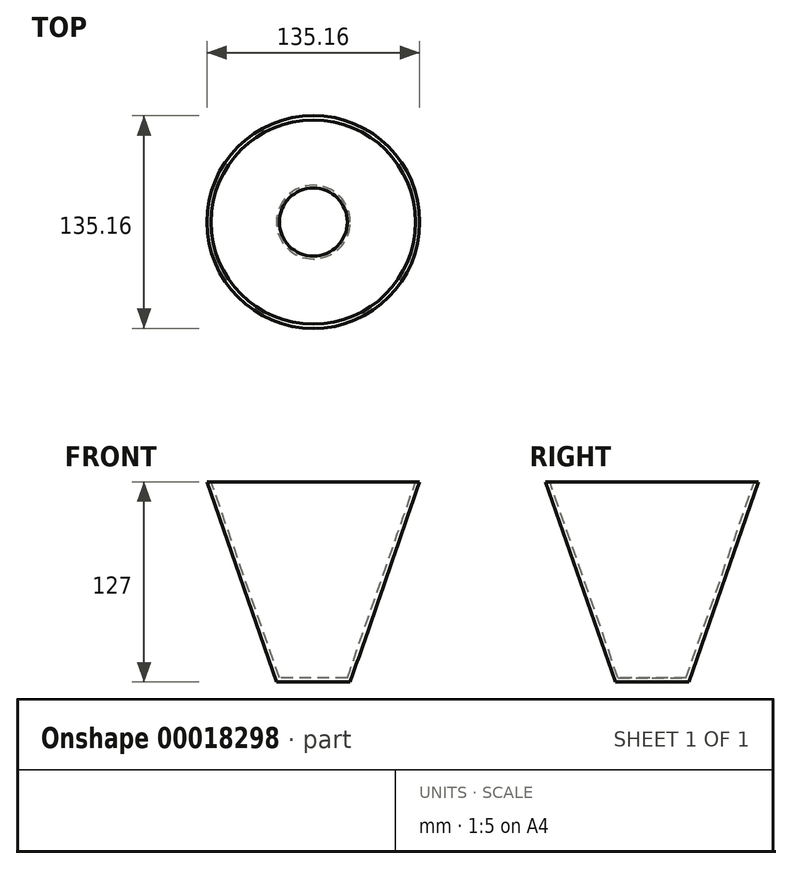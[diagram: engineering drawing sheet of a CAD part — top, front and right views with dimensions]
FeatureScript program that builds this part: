
annotation { "Feature Type Name" : "Feature", "Feature Type Description" : "" }
export const myFeature = defineFeature(function(context is Context, id is Id, definition is map)
    precondition{}
    {
        {
            var Q0;
            Q0=qCreatedBy(makeId("Top.planeOp"),FACE);
            cPlane(context, id + "F0", {"entities" : qUnion([Q0]), "cplaneType" : CPlaneType.OFFSET, "offset" : 127 * mm, "width" : 152.4 * mm, "height" : 152.4 * mm});
        }
        {
            var Q0;
            Q0=qCreatedBy(makeId("Top.planeOp"),FACE);
            var sketch = newSketch(context, id + "F1", { "sketchPlane" : qUnion([Q0])});
            skCircle(sketch, "E0", {"center": v(0, 0) * mm, "radius": 23.42 * mm});
            skSolve(sketch);
        }
        {
            var Q0;
            Q0=qCreatedBy(id+"F0.planeOp",FACE);
            var sketch = newSketch(context, id + "F2", { "sketchPlane" : qUnion([Q0])});
            skPoint(sketch, "E1", {"position": v(0, 0) * mm});
            skCircle(sketch, "E2", {"center": v(0, 0) * mm, "radius": 67.58 * mm});
            skSolve(sketch);
        }
        {
            var Q0;
            Q0=makeQuery(id+"F2.imprint","IMPRINT",FACE,{"disambiguationData":[TD([[makeQuery(id+"F2.imprint","IMPRINT",EDGE,{"derivedFrom":sQuery(id+"F2.wireOp",EDGE,"E2")}),1.0]])]});
            var Q1;
            Q1=makeQuery(id+"F1.imprint","IMPRINT",FACE,{"disambiguationData":[TD([[makeQuery(id+"F1.imprint","IMPRINT",EDGE,{"derivedFrom":sQuery(id+"F1.wireOp",EDGE,"E0")}),1.0]])]});
            loft(context, id + "F3", {"sheetProfilesArray" : [{ "sheetProfileEntities" : qUnion([Q0]) }, { "sheetProfileEntities" : qUnion([Q1]) }]});
        }
        {
            var Q0;
            Q0=makeQuery(id+"F3.opLoft","CAP_FACE",FACE,{"disambiguationData":[OSD([makeQuery(id+"F2.imprint","IMPRINT",FACE,{"disambiguationData":[TD([[makeQuery(id+"F2.imprint","IMPRINT",EDGE,{"derivedFrom":sQuery(id+"F2.wireOp",EDGE,"E2")}),1.0]])]})])],"isStart":true});
            shell(context, id + "F4", {"entities" : qUnion([Q0]), "thickness" : 2.54 * mm});
        }
        {
            var Q0;
            Q0=qCreatedBy(makeId("Right.planeOp"),FACE);
            var sketch = newSketch(context, id + "F5", { "sketchPlane" : qUnion([Q0])});
            skFitSpline(sketch, "E3", {"points": [v(-54.18, 102.94) * mm, v(-85.76, 70.05) * mm, v(-68.05, 51.82) * mm, v(-70.4, 25.65) * mm, v(-29.31, 29) * mm], "startDerivative": vector(-177.31, -127.7) * mm, "endDerivative": vector(207.17, 54.25) * mm});
            skSolve(sketch);
        }
        {
            var Q0;
            Q0=sQuery(id+"F5.wireOp",EDGE,"E3");
            extrude(context, id + "F6", {"bodyType" : ToolBodyType.SURFACE, "surfaceEntities" : qUnion([Q0]), "depth" : 14.4 * mm});
        }
    });
